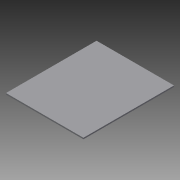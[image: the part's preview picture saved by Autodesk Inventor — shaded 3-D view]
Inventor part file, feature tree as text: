
AUTODESK INVENTOR PART (.ipt)
format: ipt  version: 2014 (Build 180170000, 170)  size: 67,072 bytes
history: native  units: in
note: dims shown in document units (in); Inventor stores cm internally (conversion verified against a paired STEP export)
features: extrude x1, sketch x1
ambient origin geometry x8: Origin, YZ Plane, XZ Plane, XY Plane, X Axis, Y Axis, Z Axis, Center Point
bodies: Solid1 (feature_tree)
feature tree (2):
  extrude  "Extrusion1"  Depth=14.75in
  sketch  "Sketch1"  dims[d0=17.25in d1=14.75in d2=0.25in d3=0.0in]
